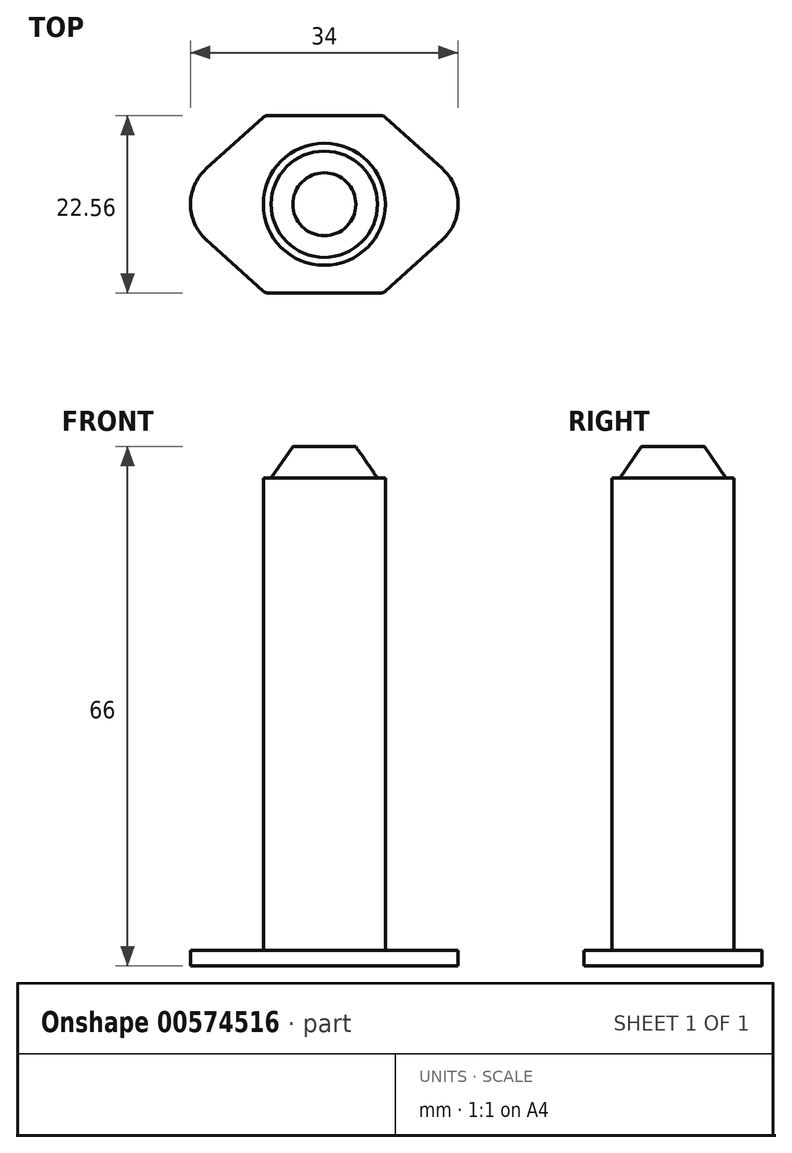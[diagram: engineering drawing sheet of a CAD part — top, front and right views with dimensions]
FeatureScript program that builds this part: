
annotation { "Feature Type Name" : "Feature", "Feature Type Description" : "" }
export const myFeature = defineFeature(function(context is Context, id is Id, definition is map)
    precondition{}
    {
        {
            var Q0;
            Q0=qCreatedBy(makeId("Front.planeOp"),FACE);
            var sketch = newSketch(context, id + "F0", { "sketchPlane" : qUnion([Q0])});
            skLineSegment(sketch, "E0", {"start": v(0, 0) * mm, "end": v(-17, 0) * mm});
            skLineSegment(sketch, "E1", {"start": v(-17, 0) * mm, "end": v(-17, 2) * mm});
            skLineSegment(sketch, "E2", {"start": v(-17, 2) * mm, "end": v(-7.75, 2) * mm});
            skLineSegment(sketch, "E3", {"start": v(-7.75, 2) * mm, "end": v(-7.75, 62) * mm});
            skLineSegment(sketch, "E4", {"start": v(-7.75, 62) * mm, "end": v(-6.75, 62) * mm});
            skLineSegment(sketch, "E5", {"start": v(-6.75, 62) * mm, "end": v(-4, 66) * mm});
            skLineSegment(sketch, "E6", {"start": v(-4, 66) * mm, "end": v(0, 66) * mm});
            skLineSegment(sketch, "E7", {"start": v(0, 66) * mm, "end": v(0, 0) * mm});
            skSolve(sketch);
        }
        {
            var Q0;
            Q0=makeQuery(id+"F0.imprint","IMPRINT",FACE,{"disambiguationData":[TD([[makeQuery(id+"F0.imprint","IMPRINT",EDGE,{"derivedFrom":sQuery(id+"F0.wireOp",EDGE,"E0")}),-1.0]])]});
            var Q1;
            Q1=sQuery(id+"F0.wireOp",EDGE,"E7");
            revolve(context, id + "F1", {"entities" : qUnion([Q0]), "axis" : qUnion([Q1]), "revolveType" : RevolveType.FULL});
        }
        {
            var Q0;
            Q0=makeQuery(id+"F1.opRevolve","SWEPT_FACE",FACE,{"disambiguationData":[OSD([sQuery(id+"F0.wireOp",EDGE,"E0")])]});
            var sketch = newSketch(context, id + "F2", { "sketchPlane" : qUnion([Q0])});
            skLineSegment(sketch, "E8.bottom", {"start": v(7.5, 11.28) * mm, "end": v(-7.5, 11.28) * mm});
            skLineSegment(sketch, "E8.top", {"start": v(7.5, -11.28) * mm, "end": v(-7.5, -11.28) * mm});
            skLineSegment(sketch, "E8.left", {"start": v(7.5, 11.28) * mm, "end": v(7.5, -11.28) * mm, "construction": true});
            skLineSegment(sketch, "E8.right", {"start": v(-7.5, 11.28) * mm, "end": v(-7.5, -11.28) * mm, "construction": true});
            skPoint(sketch, "E8.middle", {"position": v(0, 0) * mm});
            skLineSegment(sketch, "E9", {"start": v(-17, 0) * mm, "end": v(17, 0) * mm, "construction": true});
            skPoint(sketch, "E9.startSnap0", {"position": v(-7.5, 0) * mm});
            skLineSegment(sketch, "E10", {"start": v(0, 17) * mm, "end": v(0, -17) * mm, "construction": true});
            skLineSegment(sketch, "E11", {"start": v(-7.5, 11.28) * mm, "end": v(-15, 4.5) * mm});
            skArc(sketch, "E12", {"start": v(-15, 4.5) * mm, "mid": v(-16.48, 2.46) * mm, "end": v(-17, 0) * mm});
            skLineSegment(sketch, "E13.MirrorCS", {"start": v(-7.5, -11.28) * mm, "end": v(-15, -4.5) * mm});
            skArc(sketch, "E14.MirrorCS", {"start": v(-15, -4.5) * mm, "mid": v(-16.48, -2.46) * mm, "end": v(-17, 0) * mm});
            skLineSegment(sketch, "E15.MirrorCS", {"start": v(7.5, -11.28) * mm, "end": v(15, -4.5) * mm});
            skArc(sketch, "E16.MirrorCS", {"start": v(15, -4.5) * mm, "mid": v(16.48, -2.46) * mm, "end": v(17, 0) * mm});
            skArc(sketch, "E17.MirrorCS", {"start": v(15, 4.5) * mm, "mid": v(16.48, 2.46) * mm, "end": v(17, 0) * mm});
            skLineSegment(sketch, "E18.MirrorCS", {"start": v(7.5, 11.28) * mm, "end": v(15, 4.5) * mm});
            skCircle(sketch, "E19.0", {"center": v(0, 0) * mm, "radius": 17 * mm});
            skSolve(sketch);
        }
        {
            var Q0;
            Q0=makeQuery(id+"F2.imprint","IMPRINT",FACE,{"disambiguationData":[TD([[makeQuery(id+"F2.imprint","IMPRINT",EDGE,{"derivedFrom":sQuery(id+"F2.wireOp",EDGE,"E8.bottom")}),-1.0]])]});
            var Q1;
            Q1=makeQuery(id+"F2.imprint","IMPRINT",FACE,{"disambiguationData":[TD([[makeQuery(id+"F2.imprint","IMPRINT",EDGE,{"derivedFrom":sQuery(id+"F2.wireOp",EDGE,"E8.top")}),1.0]])]});
            extrude(context, id + "F3", {"entities" : qUnion([Q0, Q1]), "operationType" : NewBodyOperationType.REMOVE, "endBound" : BoundingType.THROUGH_ALL, "oppositeDirection" : true, "depth" : 25 * mm, "offsetDistance" : 25 * mm});
        }
        {
            var Q0;
            Q0=makeQuery(id+"F3.boolean.opBoolean","COPY",EDGE,{"derivedFrom":makeQuery(id+"F3.opExtrude","SWEPT_EDGE",EDGE,{"disambiguationData":[OSD([sQuery(id+"F2.wireOp",EDGE,"E8.bottom"),sQuery(id+"F2.wireOp",EDGE,"E11")])]})});
            var Q1;
            Q1=makeQuery(id+"F3.boolean.opBoolean","COPY",EDGE,{"derivedFrom":makeQuery(id+"F3.opExtrude","SWEPT_EDGE",EDGE,{"disambiguationData":[OSD([sQuery(id+"F2.wireOp",EDGE,"E8.bottom"),sQuery(id+"F2.wireOp",EDGE,"E18.MirrorCS")])]})});
            var Q2;
            Q2=makeQuery(id+"F3.boolean.opBoolean","COPY",EDGE,{"derivedFrom":makeQuery(id+"F3.opExtrude","SWEPT_EDGE",EDGE,{"disambiguationData":[OSD([sQuery(id+"F2.wireOp",EDGE,"E8.top"),sQuery(id+"F2.wireOp",EDGE,"E13.MirrorCS")])]})});
            var Q3;
            Q3=makeQuery(id+"F3.boolean.opBoolean","COPY",EDGE,{"derivedFrom":makeQuery(id+"F3.opExtrude","SWEPT_EDGE",EDGE,{"disambiguationData":[OSD([sQuery(id+"F2.wireOp",EDGE,"E8.top"),sQuery(id+"F2.wireOp",EDGE,"E15.MirrorCS")])]})});
            fillet(context, id + "F4", {"entities" : qUnion([Q0, Q1, Q2, Q3]), "radius" : 1 * mm, "tangentPropagation" : true, "allowEdgeOverflow" : false});
        }
    });
